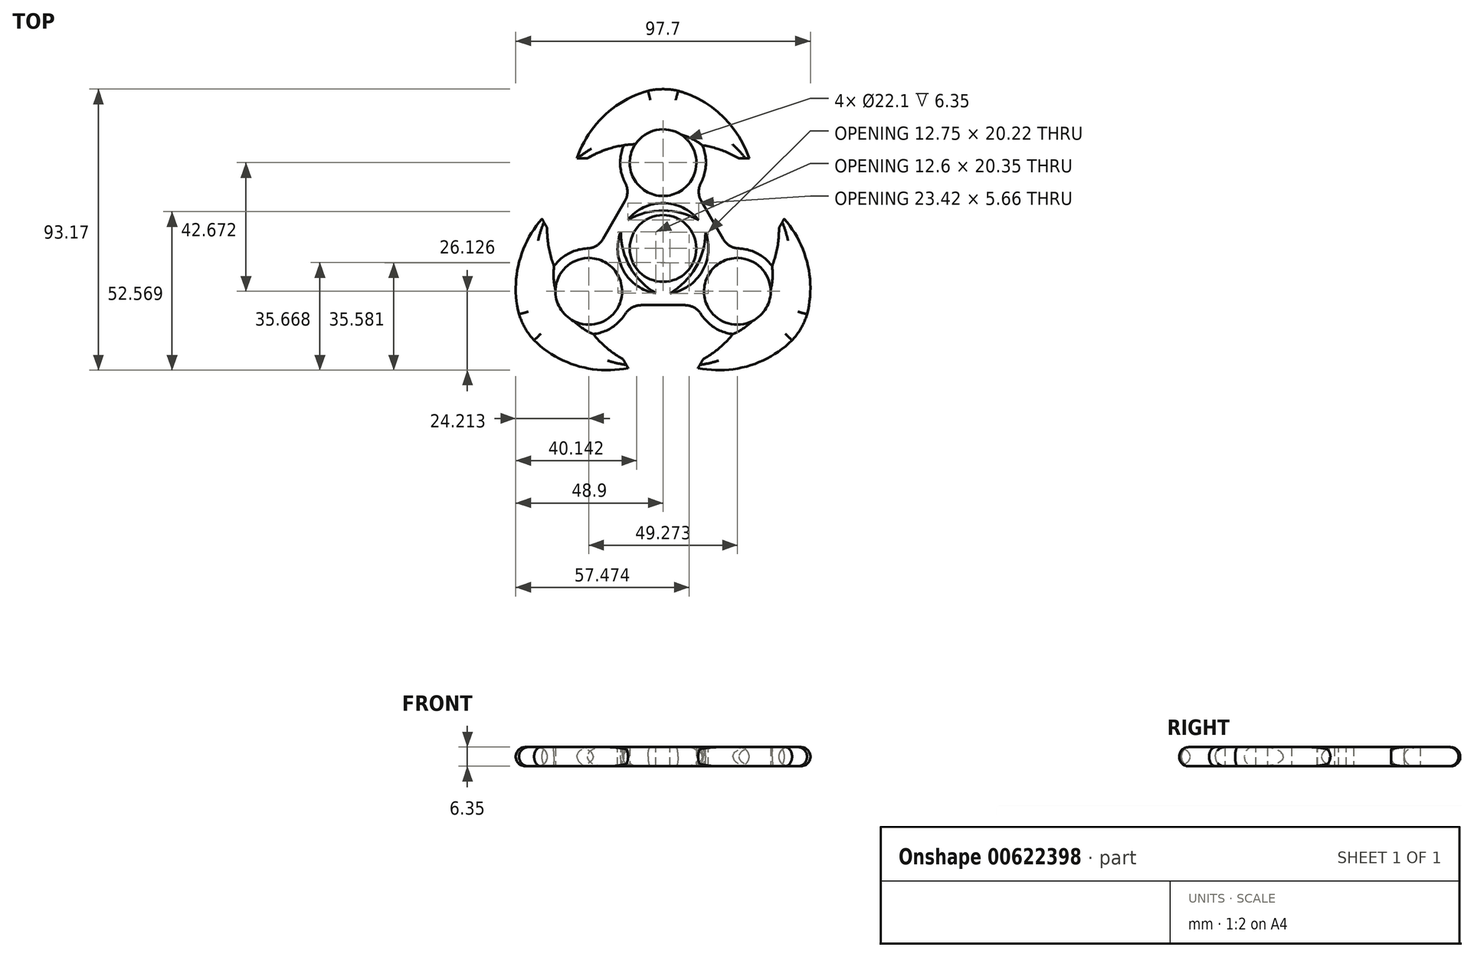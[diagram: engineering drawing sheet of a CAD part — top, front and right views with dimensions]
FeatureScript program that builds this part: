
annotation { "Feature Type Name" : "Feature", "Feature Type Description" : "" }
export const myFeature = defineFeature(function(context is Context, id is Id, definition is map)
    precondition{}
    {
        {
            var Q0;
            Q0=qCreatedBy(makeId("Top.planeOp"),FACE);
            var sketch = newSketch(context, id + "F0", { "sketchPlane" : qUnion([Q0])});
            skCircle(sketch, "E0", {"center": v(0, 28.45) * mm, "radius": 11.05 * mm});
            skCircle(sketch, "E1", {"center": v(0, 0) * mm, "radius": 11.05 * mm});
            skArc(sketch, "E2.0", {"start": v(12.57, 21.8) * mm, "mid": v(14.22, 27.96) * mm, "end": v(13, 34.23) * mm});
            skArc(sketch, "E3.trimOffspring", {"start": v(-13, 34.23) * mm, "mid": v(-14.06, 26.32) * mm, "end": v(-10.7, 19.08) * mm});
            skArc(sketch, "E4", {"start": v(25.13, 29.87) * mm, "mid": v(19.28, 32.64) * mm, "end": v(13, 34.23) * mm});
            skArc(sketch, "E5", {"start": v(28.54, 29.87) * mm, "mid": v(19.55, 44) * mm, "end": v(4.98, 52.26) * mm});
            skArc(sketch, "E6.MirrorCS", {"start": v(-28.54, 29.87) * mm, "mid": v(-19.55, 44) * mm, "end": v(-4.98, 52.26) * mm});
            skArc(sketch, "E7.MirrorCS", {"start": v(-25.13, 29.87) * mm, "mid": v(-19.28, 32.64) * mm, "end": v(-13, 34.23) * mm});
            skArc(sketch, "E8", {"start": v(4.98, 52.26) * mm, "mid": v(0, 52.82) * mm, "end": v(-4.98, 52.26) * mm});
            skLineSegment(sketch, "E9", {"start": v(25.13, 29.87) * mm, "end": v(28.54, 29.87) * mm});
            skArc(sketch, "E10.MirrorCS", {"start": v(-10.7, 19.08) * mm, "mid": v(-14.06, 26.32) * mm, "end": v(-13, 34.23) * mm});
            skLineSegment(sketch, "E11.MirrorCS", {"start": v(-25.13, 29.87) * mm, "end": v(-28.54, 29.87) * mm});
            skArc(sketch, "E12.MirrorCS", {"start": v(-12.57, 21.8) * mm, "mid": v(-14.22, 27.96) * mm, "end": v(-13, 34.23) * mm});
            skLineSegment(sketch, "E13.1.1", {"start": v(-13.3, -36.7) * mm, "end": v(-11.6, -39.65) * mm});
            skArc(sketch, "E13.1.2", {"start": v(-11.6, -39.65) * mm, "mid": v(-28.33, -38.94) * mm, "end": v(-42.77, -30.44) * mm});
            skArc(sketch, "E13.1.3", {"start": v(-47.75, -21.82) * mm, "mid": v(-45.75, -26.41) * mm, "end": v(-42.77, -30.44) * mm});
            skArc(sketch, "E13.1.4", {"start": v(-13.3, -36.7) * mm, "mid": v(-18.63, -33.02) * mm, "end": v(-23.14, -28.37) * mm});
            skArc(sketch, "E13.1.5", {"start": v(-40.14, 9.78) * mm, "mid": v(-47.89, -5.07) * mm, "end": v(-47.75, -21.82) * mm});
            skLineSegment(sketch, "E13.1.6", {"start": v(-38.43, 6.83) * mm, "end": v(-40.14, 9.78) * mm});
            skArc(sketch, "E13.1.7", {"start": v(-38.43, 6.83) * mm, "mid": v(-37.9, 0.37) * mm, "end": v(-36.14, -5.86) * mm});
            skArc(sketch, "E13.1.8", {"start": v(-25.16, 0) * mm, "mid": v(-31.32, -1.67) * mm, "end": v(-36.14, -5.86) * mm});
            skCircle(sketch, "E13.1.9", {"center": v(-24.64, -14.22) * mm, "radius": 11.05 * mm});
            skArc(sketch, "E13.1.10", {"start": v(-12.59, -21.78) * mm, "mid": v(-17.1, -26.3) * mm, "end": v(-23.14, -28.37) * mm});
            skLineSegment(sketch, "E13.2.1", {"start": v(38.43, 6.83) * mm, "end": v(40.14, 9.78) * mm});
            skArc(sketch, "E13.2.2", {"start": v(40.14, 9.78) * mm, "mid": v(47.89, -5.07) * mm, "end": v(47.75, -21.82) * mm});
            skArc(sketch, "E13.2.3", {"start": v(42.77, -30.44) * mm, "mid": v(45.75, -26.41) * mm, "end": v(47.75, -21.82) * mm});
            skArc(sketch, "E13.2.4", {"start": v(38.43, 6.83) * mm, "mid": v(37.9, 0.37) * mm, "end": v(36.14, -5.86) * mm});
            skArc(sketch, "E13.2.5", {"start": v(11.6, -39.65) * mm, "mid": v(28.33, -38.94) * mm, "end": v(42.77, -30.44) * mm});
            skLineSegment(sketch, "E13.2.6", {"start": v(13.3, -36.7) * mm, "end": v(11.6, -39.65) * mm});
            skArc(sketch, "E13.2.7", {"start": v(13.3, -36.7) * mm, "mid": v(18.63, -33.02) * mm, "end": v(23.14, -28.37) * mm});
            skArc(sketch, "E13.2.8", {"start": v(12.59, -21.78) * mm, "mid": v(17.1, -26.3) * mm, "end": v(23.14, -28.37) * mm});
            skCircle(sketch, "E13.2.9", {"center": v(24.64, -14.22) * mm, "radius": 11.05 * mm});
            skArc(sketch, "E13.2.10", {"start": v(25.16, 0) * mm, "mid": v(31.32, -1.67) * mm, "end": v(36.14, -5.86) * mm});
            skLineSegment(sketch, "E14", {"start": v(-19.89, 3.16) * mm, "end": v(-12.68, 15.64) * mm});
            skLineSegment(sketch, "E15", {"start": v(12.68, 15.64) * mm, "end": v(19.89, 3.16) * mm});
            skLineSegment(sketch, "E16", {"start": v(7.2, -18.8) * mm, "end": v(-7.2, -18.8) * mm});
            skPoint(sketch, "E17.visualSharp", {"position": v(-10.7, 19.08) * mm});
            skArc(sketch, "E17.filletArc", {"start": v(-12.68, 15.64) * mm, "mid": v(-11.83, 18.7) * mm, "end": v(-12.57, 21.8) * mm});
            skPoint(sketch, "E18.visualSharp", {"position": v(10.7, 19.08) * mm});
            skArc(sketch, "E18.filletArc", {"start": v(12.57, 21.8) * mm, "mid": v(11.83, 18.7) * mm, "end": v(12.68, 15.64) * mm});
            skPoint(sketch, "E19.visualSharp", {"position": v(21.87, -0.27) * mm});
            skArc(sketch, "E19.filletArc", {"start": v(19.89, 3.16) * mm, "mid": v(22.11, 0.9) * mm, "end": v(25.16, 0) * mm});
            skPoint(sketch, "E20.visualSharp", {"position": v(11.17, -18.8) * mm});
            skArc(sketch, "E20.filletArc", {"start": v(12.59, -21.78) * mm, "mid": v(10.28, -19.6) * mm, "end": v(7.2, -18.8) * mm});
            skPoint(sketch, "E21.visualSharp", {"position": v(-11.17, -18.8) * mm});
            skArc(sketch, "E21.filletArc", {"start": v(-7.2, -18.8) * mm, "mid": v(-10.28, -19.6) * mm, "end": v(-12.59, -21.78) * mm});
            skPoint(sketch, "E22.visualSharp", {"position": v(-21.87, -0.27) * mm});
            skArc(sketch, "E22.filletArc", {"start": v(-25.16, 0) * mm, "mid": v(-22.11, 0.9) * mm, "end": v(-19.89, 3.16) * mm});
            skSolve(sketch);
        }
        {
            var Q0;
            Q0 = qSketchRegion(id + "F0", true);
            extrude(context, id + "F1", {"entities" : qUnion([Q0]), "depth" : 6.35 * mm, "offsetDistance" : 25.4 * mm});
        }
        {
            var Q0;
            Q0=makeQuery(id+"F1.opExtrude","CAP_EDGE",EDGE,{"disambiguationData":[OSD([sQuery(id+"F0.wireOp",EDGE,"E6.MirrorCS")])],"isStart":false});
            var Q1;
            Q1=makeQuery(id+"F1.opExtrude","CAP_EDGE",EDGE,{"disambiguationData":[OSD([sQuery(id+"F0.wireOp",EDGE,"E8")])],"isStart":false});
            var Q2;
            Q2=makeQuery(id+"F1.opExtrude","CAP_EDGE",EDGE,{"disambiguationData":[OSD([sQuery(id+"F0.wireOp",EDGE,"E5")])],"isStart":false});
            var Q3;
            Q3=makeQuery(id+"F1.opExtrude","CAP_EDGE",EDGE,{"disambiguationData":[OSD([sQuery(id+"F0.wireOp",EDGE,"E4")])],"isStart":false});
            var Q4;
            Q4=makeQuery(id+"F1.opExtrude","CAP_EDGE",EDGE,{"disambiguationData":[OSD([sQuery(id+"F0.wireOp",EDGE,"E2.0")])],"isStart":false});
            var Q5;
            Q5=makeQuery(id+"F1.opExtrude","CAP_EDGE",EDGE,{"disambiguationData":[OSD([sQuery(id+"F0.wireOp",EDGE,"E12.MirrorCS")])],"isStart":false});
            var Q6;
            Q6=makeQuery(id+"F1.opExtrude","CAP_EDGE",EDGE,{"disambiguationData":[OSD([sQuery(id+"F0.wireOp",EDGE,"E11.MirrorCS")])],"isStart":false});
            var Q7;
            Q7=makeQuery(id+"F1.opExtrude","CAP_EDGE",EDGE,{"disambiguationData":[OSD([sQuery(id+"F0.wireOp",EDGE,"E9")])],"isStart":false});
            var Q8;
            Q8=makeQuery(id+"F1.opExtrude","CAP_EDGE",EDGE,{"disambiguationData":[OSD([sQuery(id+"F0.wireOp",EDGE,"E15")])],"isStart":false});
            var Q9;
            Q9=makeQuery(id+"F1.opExtrude","CAP_EDGE",EDGE,{"disambiguationData":[OSD([sQuery(id+"F0.wireOp",EDGE,"E13.2.10")])],"isStart":false});
            var Q10;
            Q10=makeQuery(id+"F1.opExtrude","CAP_EDGE",EDGE,{"disambiguationData":[OSD([sQuery(id+"F0.wireOp",EDGE,"E13.2.4")])],"isStart":false});
            var Q11;
            Q11=makeQuery(id+"F1.opExtrude","CAP_EDGE",EDGE,{"disambiguationData":[OSD([sQuery(id+"F0.wireOp",EDGE,"E13.2.1")])],"isStart":false});
            var Q12;
            Q12=makeQuery(id+"F1.opExtrude","CAP_EDGE",EDGE,{"disambiguationData":[OSD([sQuery(id+"F0.wireOp",EDGE,"E13.2.2")])],"isStart":false});
            var Q13;
            Q13=makeQuery(id+"F1.opExtrude","CAP_EDGE",EDGE,{"disambiguationData":[OSD([sQuery(id+"F0.wireOp",EDGE,"E13.2.3")])],"isStart":false});
            var Q14;
            Q14=makeQuery(id+"F1.opExtrude","CAP_EDGE",EDGE,{"disambiguationData":[OSD([sQuery(id+"F0.wireOp",EDGE,"E13.2.5")])],"isStart":false});
            var Q15;
            Q15=makeQuery(id+"F1.opExtrude","CAP_EDGE",EDGE,{"disambiguationData":[OSD([sQuery(id+"F0.wireOp",EDGE,"E13.2.6")])],"isStart":false});
            var Q16;
            Q16=makeQuery(id+"F1.opExtrude","CAP_EDGE",EDGE,{"disambiguationData":[OSD([sQuery(id+"F0.wireOp",EDGE,"E13.2.7")])],"isStart":false});
            var Q17;
            Q17=makeQuery(id+"F1.opExtrude","CAP_EDGE",EDGE,{"disambiguationData":[OSD([sQuery(id+"F0.wireOp",EDGE,"E13.2.8")])],"isStart":false});
            var Q18;
            Q18=makeQuery(id+"F1.opExtrude","CAP_EDGE",EDGE,{"disambiguationData":[OSD([sQuery(id+"F0.wireOp",EDGE,"E16")])],"isStart":false});
            var Q19;
            Q19=makeQuery(id+"F1.opExtrude","CAP_EDGE",EDGE,{"disambiguationData":[OSD([sQuery(id+"F0.wireOp",EDGE,"E13.1.10")])],"isStart":false});
            var Q20;
            Q20=makeQuery(id+"F1.opExtrude","CAP_EDGE",EDGE,{"disambiguationData":[OSD([sQuery(id+"F0.wireOp",EDGE,"E13.1.4")])],"isStart":false});
            var Q21;
            Q21=makeQuery(id+"F1.opExtrude","CAP_EDGE",EDGE,{"disambiguationData":[OSD([sQuery(id+"F0.wireOp",EDGE,"E13.1.1")])],"isStart":false});
            var Q22;
            Q22=makeQuery(id+"F1.opExtrude","CAP_EDGE",EDGE,{"disambiguationData":[OSD([sQuery(id+"F0.wireOp",EDGE,"E13.1.2")])],"isStart":false});
            var Q23;
            Q23=makeQuery(id+"F1.opExtrude","CAP_EDGE",EDGE,{"disambiguationData":[OSD([sQuery(id+"F0.wireOp",EDGE,"E13.1.3")])],"isStart":false});
            var Q24;
            Q24=makeQuery(id+"F1.opExtrude","CAP_EDGE",EDGE,{"disambiguationData":[OSD([sQuery(id+"F0.wireOp",EDGE,"E13.1.5")])],"isStart":false});
            var Q25;
            Q25=makeQuery(id+"F1.opExtrude","CAP_EDGE",EDGE,{"disambiguationData":[OSD([sQuery(id+"F0.wireOp",EDGE,"E13.1.7")])],"isStart":false});
            var Q26;
            Q26=makeQuery(id+"F1.opExtrude","CAP_EDGE",EDGE,{"disambiguationData":[OSD([sQuery(id+"F0.wireOp",EDGE,"E13.1.8")])],"isStart":false});
            var Q27;
            Q27=makeQuery(id+"F1.opExtrude","CAP_EDGE",EDGE,{"disambiguationData":[OSD([sQuery(id+"F0.wireOp",EDGE,"E14")])],"isStart":false});
            var Q28;
            Q28=makeQuery(id+"F1.opExtrude","CAP_EDGE",EDGE,{"disambiguationData":[OSD([sQuery(id+"F0.wireOp",EDGE,"E13.1.6")])],"isStart":false});
            var Q29;
            Q29=makeQuery(id+"F1.opExtrude","CAP_EDGE",EDGE,{"disambiguationData":[OSD([sQuery(id+"F0.wireOp",EDGE,"E7.MirrorCS")])],"isStart":false});
            var Q30;
            Q30=makeQuery(id+"F1.opExtrude","CAP_EDGE",EDGE,{"disambiguationData":[OSD([sQuery(id+"F0.wireOp",EDGE,"E15")])],"isStart":true});
            var Q31;
            Q31=makeQuery(id+"F1.opExtrude","CAP_EDGE",EDGE,{"disambiguationData":[OSD([sQuery(id+"F0.wireOp",EDGE,"E13.2.10")])],"isStart":true});
            var Q32;
            Q32=makeQuery(id+"F1.opExtrude","CAP_EDGE",EDGE,{"disambiguationData":[OSD([sQuery(id+"F0.wireOp",EDGE,"E13.2.4")])],"isStart":true});
            var Q33;
            Q33=makeQuery(id+"F1.opExtrude","CAP_EDGE",EDGE,{"disambiguationData":[OSD([sQuery(id+"F0.wireOp",EDGE,"E13.2.1")])],"isStart":true});
            var Q34;
            Q34=makeQuery(id+"F1.opExtrude","CAP_EDGE",EDGE,{"disambiguationData":[OSD([sQuery(id+"F0.wireOp",EDGE,"E13.2.2")])],"isStart":true});
            var Q35;
            Q35=makeQuery(id+"F1.opExtrude","CAP_EDGE",EDGE,{"disambiguationData":[OSD([sQuery(id+"F0.wireOp",EDGE,"E13.2.5")])],"isStart":true});
            var Q36;
            Q36=makeQuery(id+"F1.opExtrude","CAP_EDGE",EDGE,{"disambiguationData":[OSD([sQuery(id+"F0.wireOp",EDGE,"E13.2.3")])],"isStart":true});
            var Q37;
            Q37=makeQuery(id+"F1.opExtrude","CAP_EDGE",EDGE,{"disambiguationData":[OSD([sQuery(id+"F0.wireOp",EDGE,"E16")])],"isStart":true});
            var Q38;
            Q38=makeQuery(id+"F1.opExtrude","CAP_EDGE",EDGE,{"disambiguationData":[OSD([sQuery(id+"F0.wireOp",EDGE,"E13.2.8")])],"isStart":true});
            var Q39;
            Q39=makeQuery(id+"F1.opExtrude","CAP_EDGE",EDGE,{"disambiguationData":[OSD([sQuery(id+"F0.wireOp",EDGE,"E13.2.7")])],"isStart":true});
            var Q40;
            Q40=makeQuery(id+"F1.opExtrude","CAP_EDGE",EDGE,{"disambiguationData":[OSD([sQuery(id+"F0.wireOp",EDGE,"E13.2.7")])],"isStart":true});
            var Q41;
            Q41=makeQuery(id+"F1.opExtrude","CAP_EDGE",EDGE,{"disambiguationData":[OSD([sQuery(id+"F0.wireOp",EDGE,"E13.2.6")])],"isStart":true});
            var Q42;
            Q42=makeQuery(id+"F1.opExtrude","CAP_EDGE",EDGE,{"disambiguationData":[OSD([sQuery(id+"F0.wireOp",EDGE,"E13.1.1")])],"isStart":true});
            var Q43;
            Q43=makeQuery(id+"F1.opExtrude","CAP_EDGE",EDGE,{"disambiguationData":[OSD([sQuery(id+"F0.wireOp",EDGE,"E13.1.4")])],"isStart":true});
            var Q44;
            Q44=makeQuery(id+"F1.opExtrude","CAP_EDGE",EDGE,{"disambiguationData":[OSD([sQuery(id+"F0.wireOp",EDGE,"E13.1.8")])],"isStart":true});
            var Q45;
            Q45=makeQuery(id+"F1.opExtrude","CAP_EDGE",EDGE,{"disambiguationData":[OSD([sQuery(id+"F0.wireOp",EDGE,"E13.1.7")])],"isStart":true});
            var Q46;
            Q46=makeQuery(id+"F1.opExtrude","CAP_EDGE",EDGE,{"disambiguationData":[OSD([sQuery(id+"F0.wireOp",EDGE,"E13.1.2")])],"isStart":true});
            var Q47;
            Q47=makeQuery(id+"F1.opExtrude","CAP_EDGE",EDGE,{"disambiguationData":[OSD([sQuery(id+"F0.wireOp",EDGE,"E13.1.3")])],"isStart":true});
            var Q48;
            Q48=makeQuery(id+"F1.opExtrude","CAP_EDGE",EDGE,{"disambiguationData":[OSD([sQuery(id+"F0.wireOp",EDGE,"E13.1.5")])],"isStart":true});
            var Q49;
            Q49=makeQuery(id+"F1.opExtrude","CAP_EDGE",EDGE,{"disambiguationData":[OSD([sQuery(id+"F0.wireOp",EDGE,"E12.MirrorCS")])],"isStart":true});
            var Q50;
            Q50=makeQuery(id+"F1.opExtrude","CAP_EDGE",EDGE,{"disambiguationData":[OSD([sQuery(id+"F0.wireOp",EDGE,"E14")])],"isStart":true});
            var Q51;
            Q51=makeQuery(id+"F1.opExtrude","CAP_EDGE",EDGE,{"disambiguationData":[OSD([sQuery(id+"F0.wireOp",EDGE,"E11.MirrorCS")])],"isStart":true});
            var Q52;
            Q52=makeQuery(id+"F1.opExtrude","CAP_EDGE",EDGE,{"disambiguationData":[OSD([sQuery(id+"F0.wireOp",EDGE,"E8")])],"isStart":true});
            var Q53;
            Q53=makeQuery(id+"F1.opExtrude","CAP_EDGE",EDGE,{"disambiguationData":[OSD([sQuery(id+"F0.wireOp",EDGE,"E5")])],"isStart":true});
            var Q54;
            Q54=makeQuery(id+"F1.opExtrude","CAP_EDGE",EDGE,{"disambiguationData":[OSD([sQuery(id+"F0.wireOp",EDGE,"E4")])],"isStart":true});
            var Q55;
            Q55=makeQuery(id+"F1.opExtrude","CAP_EDGE",EDGE,{"disambiguationData":[OSD([sQuery(id+"F0.wireOp",EDGE,"E9")])],"isStart":true});
            var Q56;
            Q56=makeQuery(id+"F1.opExtrude","CAP_EDGE",EDGE,{"disambiguationData":[OSD([sQuery(id+"F0.wireOp",EDGE,"E2.0")])],"isStart":true});
            var Q57;
            Q57=makeQuery(id+"F1.opExtrude","CAP_EDGE",EDGE,{"disambiguationData":[OSD([sQuery(id+"F0.wireOp",EDGE,"E6.MirrorCS")])],"isStart":true});
            var Q58;
            Q58=makeQuery(id+"F1.opExtrude","CAP_EDGE",EDGE,{"disambiguationData":[OSD([sQuery(id+"F0.wireOp",EDGE,"E13.1.6")])],"isStart":true});
            var Q59;
            Q59=makeQuery(id+"F1.opExtrude","CAP_EDGE",EDGE,{"disambiguationData":[OSD([sQuery(id+"F0.wireOp",EDGE,"E13.1.10")])],"isStart":true});
            var Q60;
            Q60=makeQuery(id+"F1.opExtrude","CAP_EDGE",EDGE,{"disambiguationData":[OSD([sQuery(id+"F0.wireOp",EDGE,"E7.MirrorCS")])],"isStart":true});
            fillet(context, id + "F2", {"entities" : qUnion([Q0, Q1, Q2, Q3, Q4, Q5, Q6, Q7, Q8, Q9, Q10, Q11, Q12, Q13, Q14, Q15, Q16, Q17, Q18, Q19, Q20, Q21, Q22, Q23, Q24, Q25, Q26, Q27, Q28, Q29, Q30, Q31, Q32, Q33, Q34, Q35, Q36, Q37, Q38, Q39, Q40, Q41, Q42, Q43, Q44, Q45, Q46, Q47, Q48, Q49, Q50, Q51, Q52, Q53, Q54, Q55, Q56, Q57, Q58, Q59, Q60]), "radius" : 3.17 * mm, "tangentPropagation" : true, "allowEdgeOverflow" : false});
        }
        {
            var Q0;
            Q0=makeQuery(id+"F2.opFillet","SPLIT",FACE,{"disambiguationData":[OD(0.0)],"derivedFrom":makeQuery(id+"F1.opExtrude","CAP_FACE",FACE,{"disambiguationData":[OSD([sQuery(id+"F0.wireOp",EDGE,"E0"),sQuery(id+"F0.wireOp",EDGE,"E2.0"),sQuery(id+"F0.wireOp",EDGE,"E4"),sQuery(id+"F0.wireOp",EDGE,"E5"),sQuery(id+"F0.wireOp",EDGE,"E8"),sQuery(id+"F0.wireOp",EDGE,"E9"),sQuery(id+"F0.wireOp",EDGE,"E11.MirrorCS"),sQuery(id+"F0.wireOp",EDGE,"E12.MirrorCS"),sQuery(id+"F0.wireOp",EDGE,"E6.MirrorCS"),sQuery(id+"F0.wireOp",EDGE,"E7.MirrorCS"),sQuery(id+"F0.wireOp",EDGE,"E13.1.1"),sQuery(id+"F0.wireOp",EDGE,"E13.1.2"),sQuery(id+"F0.wireOp",EDGE,"E13.1.3"),sQuery(id+"F0.wireOp",EDGE,"E13.1.4"),sQuery(id+"F0.wireOp",EDGE,"E13.1.5"),sQuery(id+"F0.wireOp",EDGE,"E13.1.6"),sQuery(id+"F0.wireOp",EDGE,"E13.1.7"),sQuery(id+"F0.wireOp",EDGE,"E13.1.8"),sQuery(id+"F0.wireOp",EDGE,"E13.1.9"),sQuery(id+"F0.wireOp",EDGE,"E13.1.10"),sQuery(id+"F0.wireOp",EDGE,"E1"),sQuery(id+"F0.wireOp",EDGE,"E13.2.1"),sQuery(id+"F0.wireOp",EDGE,"E13.2.2"),sQuery(id+"F0.wireOp",EDGE,"E13.2.3"),sQuery(id+"F0.wireOp",EDGE,"E13.2.4"),sQuery(id+"F0.wireOp",EDGE,"E13.2.5"),sQuery(id+"F0.wireOp",EDGE,"E13.2.6"),sQuery(id+"F0.wireOp",EDGE,"E13.2.7"),sQuery(id+"F0.wireOp",EDGE,"E13.2.8"),sQuery(id+"F0.wireOp",EDGE,"E13.2.9"),sQuery(id+"F0.wireOp",EDGE,"E13.2.10"),sQuery(id+"F0.wireOp",EDGE,"E14"),sQuery(id+"F0.wireOp",EDGE,"E15"),sQuery(id+"F0.wireOp",EDGE,"E16"),sQuery(id+"F0.wireOp",EDGE,"E17.filletArc"),sQuery(id+"F0.wireOp",EDGE,"E18.filletArc"),sQuery(id+"F0.wireOp",EDGE,"E19.filletArc"),sQuery(id+"F0.wireOp",EDGE,"E20.filletArc"),sQuery(id+"F0.wireOp",EDGE,"E21.filletArc"),sQuery(id+"F0.wireOp",EDGE,"E22.filletArc")])],"isStart":false})});
            var sketch = newSketch(context, id + "F3", { "sketchPlane" : qUnion([Q0])});
            skArc(sketch, "E23.0", {"start": v(11.76, 9.39) * mm, "mid": v(0.08, 15.05) * mm, "end": v(-11.66, 9.51) * mm});
            skArc(sketch, "E24", {"start": v(11.76, 9.39) * mm, "mid": v(0.07, 12.56) * mm, "end": v(-11.66, 9.51) * mm});
            skArc(sketch, "E25.1.0", {"start": v(-14.01, 5.5) * mm, "mid": v(-10.9, -6.22) * mm, "end": v(-2.4, -14.86) * mm});
            skArc(sketch, "E25.1.1", {"start": v(-14.01, 5.5) * mm, "mid": v(-13.07, -7.46) * mm, "end": v(-2.4, -14.86) * mm});
            skArc(sketch, "E25.2.0", {"start": v(2.25, -14.88) * mm, "mid": v(10.84, -6.34) * mm, "end": v(14.07, 5.34) * mm});
            skArc(sketch, "E25.2.1", {"start": v(2.25, -14.88) * mm, "mid": v(13, -7.6) * mm, "end": v(14.07, 5.34) * mm});
            skSolve(sketch);
        }
        {
            var Q0;
            Q0=makeQuery(id+"F3.imprint","IMPRINT",FACE,{"disambiguationData":[TD([[makeQuery(id+"F3.imprint","IMPRINT",EDGE,{"derivedFrom":sQuery(id+"F3.wireOp",EDGE,"E23.0")}),1.0]])]});
            var Q1;
            Q1=makeQuery(id+"F3.imprint","IMPRINT",FACE,{"disambiguationData":[TD([[makeQuery(id+"F3.imprint","IMPRINT",EDGE,{"derivedFrom":sQuery(id+"F3.wireOp",EDGE,"E25.1.0")}),-1.0]])]});
            var Q2;
            Q2=makeQuery(id+"F3.imprint","IMPRINT",FACE,{"disambiguationData":[TD([[makeQuery(id+"F3.imprint","IMPRINT",EDGE,{"derivedFrom":sQuery(id+"F3.wireOp",EDGE,"E25.2.0")}),-1.0]])]});
            extrude(context, id + "F4", {"entities" : qUnion([Q0, Q1, Q2]), "operationType" : NewBodyOperationType.REMOVE, "oppositeDirection" : true, "depth" : 6.35 * mm, "offsetDistance" : 25.4 * mm});
        }
    });
